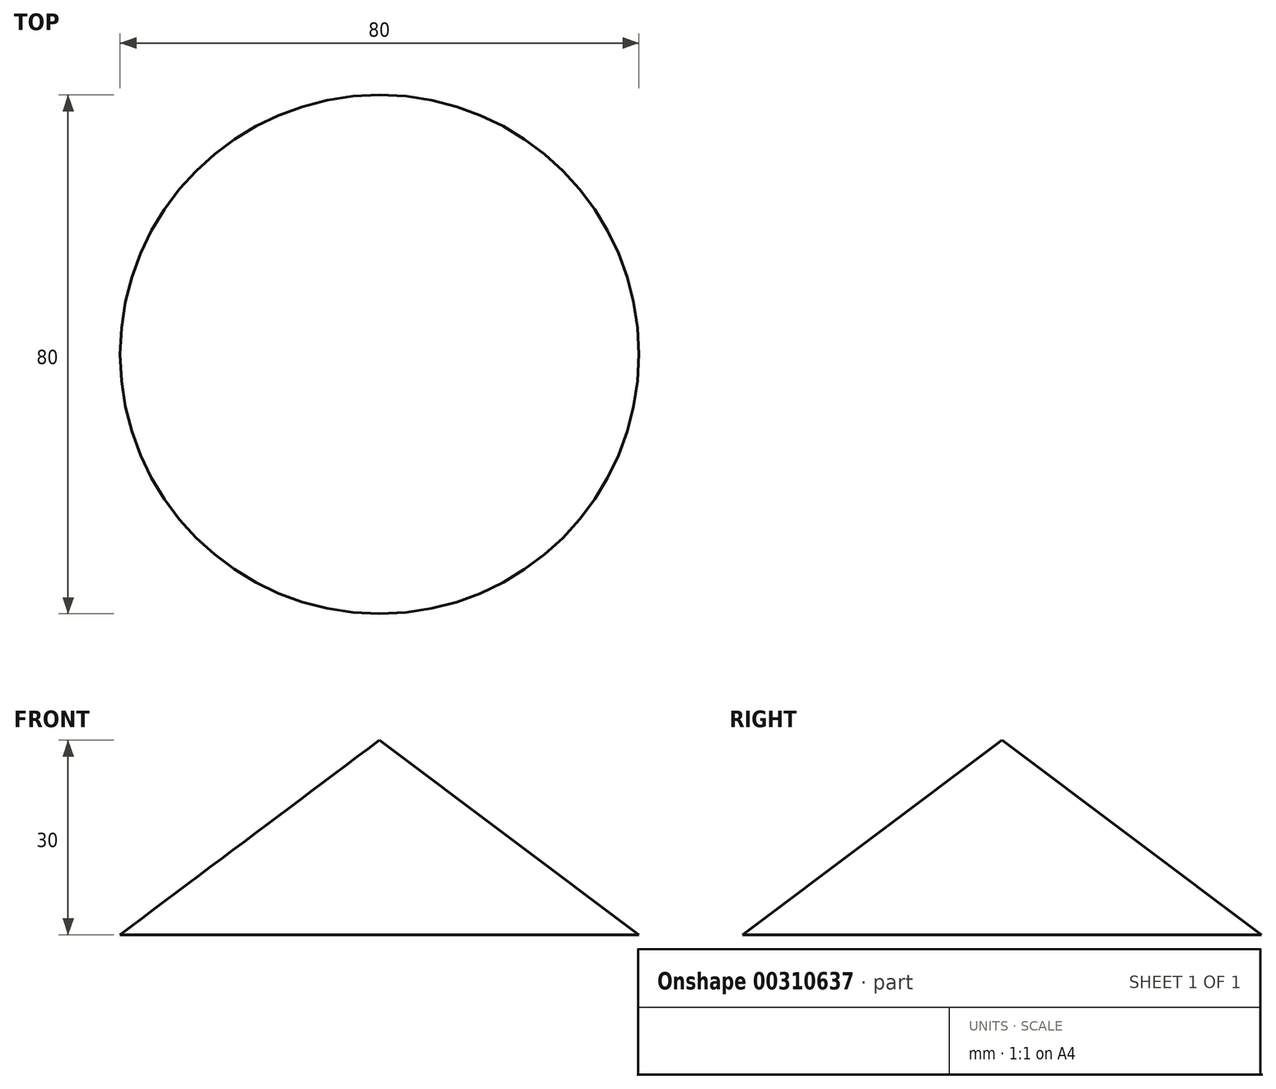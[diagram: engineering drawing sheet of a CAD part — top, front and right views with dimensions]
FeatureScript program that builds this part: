
annotation { "Feature Type Name" : "Feature", "Feature Type Description" : "" }
export const myFeature = defineFeature(function(context is Context, id is Id, definition is map)
    precondition{}
    {
        {
            var Q0;
            Q0=qCreatedBy(makeId("Front.planeOp"),FACE);
            var sketch = newSketch(context, id + "F0", { "sketchPlane" : qUnion([Q0])});
            skLineSegment(sketch, "E0", {"start": v(0, 0) * mm, "end": v(0, 30) * mm});
            skLineSegment(sketch, "E1", {"start": v(0, 30) * mm, "end": v(40, 0) * mm});
            skLineSegment(sketch, "E2", {"start": v(40, 0) * mm, "end": v(0, 0) * mm});
            skLineSegment(sketch, "E3", {"start": v(0, 33.6) * mm, "end": v(0, -7.66) * mm, "construction": true});
            skSolve(sketch);
        }
        {
            var Q0;
            Q0=makeQuery(id+"F0.imprint","IMPRINT",FACE,{"disambiguationData":[TD([[makeQuery(id+"F0.imprint","IMPRINT",EDGE,{"derivedFrom":sQuery(id+"F0.wireOp",EDGE,"E0")}),-1.0]])]});
            var Q1;
            Q1=sQuery(id+"F0.wireOp",EDGE,"E0");
            revolve(context, id + "F1", {"entities" : qUnion([Q0]), "axis" : qUnion([Q1]), "revolveType" : RevolveType.FULL});
        }
    });
